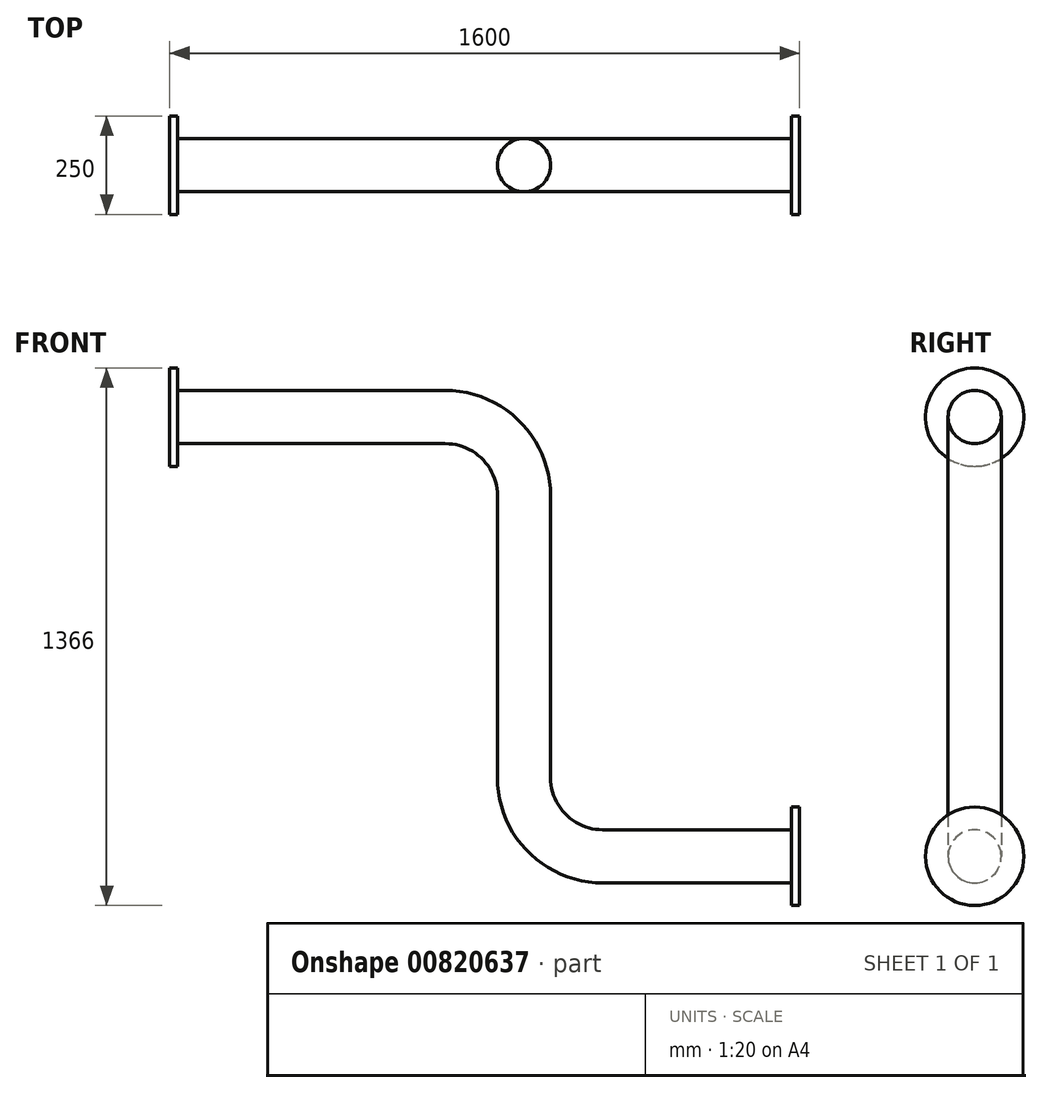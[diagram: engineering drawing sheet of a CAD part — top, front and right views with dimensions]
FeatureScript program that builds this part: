
annotation { "Feature Type Name" : "Feature", "Feature Type Description" : "" }
export const myFeature = defineFeature(function(context is Context, id is Id, definition is map)
    precondition{}
    {
        {
            var Q0;
            Q0=qCreatedBy(makeId("Front.planeOp"),FACE);
            var sketch = newSketch(context, id + "F0", { "sketchPlane" : qUnion([Q0])});
            skLineSegment(sketch, "E0", {"start": v(0, 0) * mm, "end": v(700, 0) * mm});
            skLineSegment(sketch, "E1", {"start": v(900, -200) * mm, "end": v(900, -916) * mm});
            skLineSegment(sketch, "E2", {"start": v(1100, -1116) * mm, "end": v(1600, -1116) * mm});
            skPoint(sketch, "E3.visualSharp", {"position": v(900, 0) * mm});
            skArc(sketch, "E3.filletArc", {"start": v(900, -200) * mm, "mid": v(841.42, -58.58) * mm, "end": v(700, 0) * mm});
            skPoint(sketch, "E4.visualSharp", {"position": v(900, -1116) * mm});
            skArc(sketch, "E4.filletArc", {"start": v(900, -916) * mm, "mid": v(958.58, -1057.42) * mm, "end": v(1100, -1116) * mm});
            skSolve(sketch);
        }
        {
            var Q0;
            Q0=qCreatedBy(makeId("Right.planeOp"),FACE);
            var sketch = newSketch(context, id + "F1", { "sketchPlane" : qUnion([Q0])});
            skCircle(sketch, "E5", {"center": v(0, 0) * mm, "radius": 67.5 * mm});
            skCircle(sketch, "E6", {"center": v(0, 0) * mm, "radius": 125 * mm});
            skSolve(sketch);
        }
        {
            var Q0;
            Q0=makeQuery(id+"F1.imprint","IMPRINT",FACE,{"disambiguationData":[TD([[makeQuery(id+"F1.imprint","IMPRINT",EDGE,{"derivedFrom":sQuery(id+"F1.wireOp",EDGE,"E5")}),1.0]])]});
            var Q1;
            Q1=sQuery(id+"F0.wireOp",EDGE,"E0");
            var Q2;
            Q2=sQuery(id+"F0.wireOp",EDGE,"E3.filletArc");
            var Q3;
            Q3=sQuery(id+"F0.wireOp",EDGE,"E1");
            var Q4;
            Q4=sQuery(id+"F0.wireOp",EDGE,"E4.filletArc");
            var Q5;
            Q5=sQuery(id+"F0.wireOp",EDGE,"E2");
            sweep(context, id + "F2", {"profiles" : qUnion([Q0]), "path" : qUnion([Q1, Q2, Q3, Q4, Q5])});
        }
        {
            var Q0;
            Q0=makeQuery(id+"F1.imprint","IMPRINT",FACE,{"disambiguationData":[TD([[makeQuery(id+"F1.imprint","IMPRINT",EDGE,{"derivedFrom":sQuery(id+"F1.wireOp",EDGE,"E5")}),-1.0]])]});
            extrude(context, id + "F3", {"entities" : qUnion([Q0]), "operationType" : NewBodyOperationType.ADD, "depth" : 20 * mm, "offsetDistance" : 25 * mm});
        }
        {
            var Q0;
            Q0=makeQuery(id+"F2.opSweep","CAP_FACE",FACE,{"disambiguationData":[OSD([sQuery(id+"F0.wireOp",VERTEX,"E2.end"),sQuery(id+"F1.wireOp",EDGE,"E5")])],"isStart":false});
            var sketch = newSketch(context, id + "F4", { "sketchPlane" : qUnion([Q0])});
            skCircle(sketch, "E7", {"center": v(0, -1116) * mm, "radius": 125 * mm});
            skSolve(sketch);
        }
        {
            var Q0;
            Q0=makeQuery(id+"F4.imprint","IMPRINT",FACE,{"disambiguationData":[TD([[makeQuery(id+"F4.imprint","IMPRINT",EDGE,{"derivedFrom":sQuery(id+"F4.wireOp",EDGE,"E7")}),1.0]])]});
            extrude(context, id + "F5", {"entities" : qUnion([Q0]), "operationType" : NewBodyOperationType.ADD, "oppositeDirection" : true, "depth" : 20 * mm, "offsetDistance" : 25 * mm});
        }
    });
